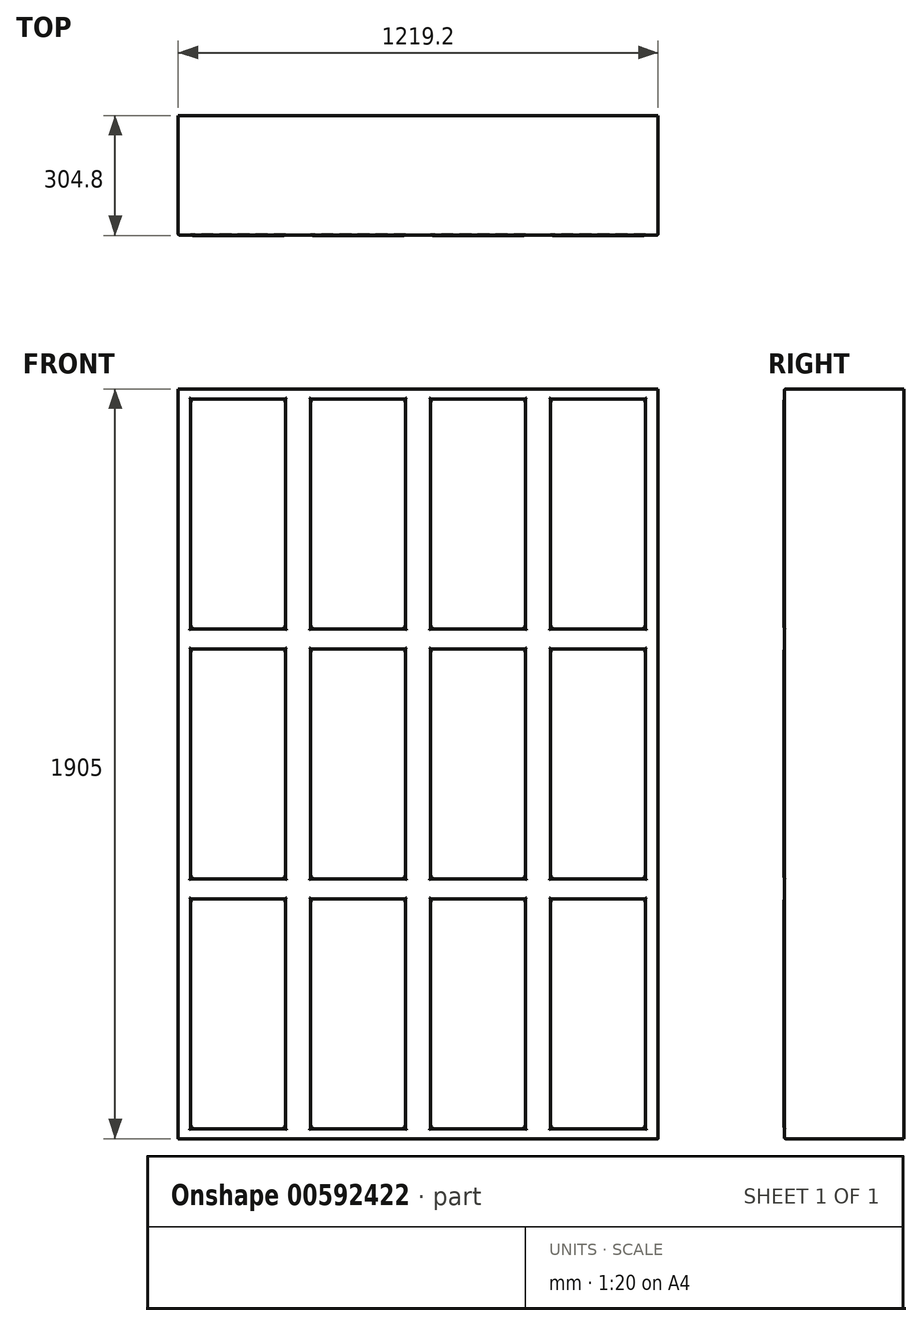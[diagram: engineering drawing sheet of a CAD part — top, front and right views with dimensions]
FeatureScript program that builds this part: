
annotation { "Feature Type Name" : "Feature", "Feature Type Description" : "" }
export const myFeature = defineFeature(function(context is Context, id is Id, definition is map)
    precondition{}
    {
        {
            var Q0;
            Q0=qCreatedBy(makeId("Top.planeOp"),FACE);
            var sketch = newSketch(context, id + "F0", { "sketchPlane" : qUnion([Q0])});
            skLineSegment(sketch, "E0.bottom", {"start": v(609.6, -148.59) * mm, "end": v(-609.6, -148.6) * mm});
            skLineSegment(sketch, "E0.top", {"start": v(609.6, 148.6) * mm, "end": v(-609.6, 148.59) * mm});
            skLineSegment(sketch, "E0.left", {"start": v(609.6, -148.59) * mm, "end": v(609.6, 148.6) * mm});
            skLineSegment(sketch, "E0.right", {"start": v(-609.6, -148.6) * mm, "end": v(-609.6, 148.59) * mm});
            skPoint(sketch, "E0.middle", {"position": v(0, 0) * mm});
            skSolve(sketch);
        }
        {
            var Q0;
            Q0=makeQuery(id+"F0.imprint","IMPRINT",FACE,{"disambiguationData":[TD([[makeQuery(id+"F0.imprint","IMPRINT",EDGE,{"derivedFrom":sQuery(id+"F0.wireOp",EDGE,"E0.bottom")}),-1.0]])]});
            extrude(context, id + "F1", {"entities" : qUnion([Q0]), "depth" : 1905 * mm, "offsetDistance" : 25.4 * mm});
        }
        {
            var Q0;
            Q0=makeQuery(id+"F1.opExtrude","SWEPT_FACE",FACE,{"disambiguationData":[OSD([sQuery(id+"F0.wireOp",EDGE,"E0.bottom")])]});
            var sketch = newSketch(context, id + "F2", { "sketchPlane" : qUnion([Q0])});
            skLineSegment(sketch, "E1.bottom", {"start": v(-609.6, 1905) * mm, "end": v(-304.8, 1905) * mm});
            skLineSegment(sketch, "E1.top", {"start": v(-609.6, 1270) * mm, "end": v(-304.8, 1270) * mm});
            skLineSegment(sketch, "E1.left", {"start": v(-609.6, 1905) * mm, "end": v(-609.6, 1270) * mm});
            skLineSegment(sketch, "E1.right", {"start": v(-304.8, 1905) * mm, "end": v(-304.8, 1270) * mm});
            skLineSegment(sketch, "E2.bottom", {"start": v(-336.55, 1295.4) * mm, "end": v(-577.85, 1295.4) * mm});
            skLineSegment(sketch, "E2.top", {"start": v(-336.55, 1879.6) * mm, "end": v(-577.85, 1879.6) * mm});
            skLineSegment(sketch, "E2.left", {"start": v(-336.55, 1295.4) * mm, "end": v(-336.55, 1879.6) * mm});
            skLineSegment(sketch, "E2.right", {"start": v(-577.85, 1295.4) * mm, "end": v(-577.85, 1879.6) * mm});
            skPoint(sketch, "E2.middle", {"position": v(-457.2, 1587.5) * mm});
            skPoint(sketch, "E2.middle.positionSnap0", {"position": v(-304.8, 1587.5) * mm});
            skPoint(sketch, "E2.middle.positionSnap1", {"position": v(-457.2, 1270) * mm});
            skPoint(sketch, "E2.centerSnap0", {"position": v(-304.8, 1587.5) * mm});
            skPoint(sketch, "E2.centerSnap1", {"position": v(-457.2, 1270) * mm});
            skLineSegment(sketch, "E3.0.1.0", {"start": v(-304.8, 1270) * mm, "end": v(-304.8, 635) * mm});
            skLineSegment(sketch, "E3.0.1.1", {"start": v(-609.6, 635) * mm, "end": v(-304.8, 635) * mm});
            skLineSegment(sketch, "E3.0.1.2", {"start": v(-336.55, 660.4) * mm, "end": v(-336.55, 1244.6) * mm});
            skLineSegment(sketch, "E3.0.1.3", {"start": v(-577.85, 660.4) * mm, "end": v(-577.85, 1244.6) * mm});
            skLineSegment(sketch, "E3.0.1.4", {"start": v(-336.55, 1244.6) * mm, "end": v(-577.85, 1244.6) * mm});
            skLineSegment(sketch, "E3.0.1.5", {"start": v(-336.55, 660.4) * mm, "end": v(-577.85, 660.4) * mm});
            skLineSegment(sketch, "E3.0.1.7", {"start": v(-609.6, 1270) * mm, "end": v(-609.6, 635) * mm});
            skLineSegment(sketch, "E3.0.2.0", {"start": v(-304.8, 635) * mm, "end": v(-304.8, 0) * mm});
            skLineSegment(sketch, "E3.0.2.1", {"start": v(-609.6, 0) * mm, "end": v(-304.8, 0) * mm});
            skLineSegment(sketch, "E3.0.2.2", {"start": v(-336.55, 25.4) * mm, "end": v(-336.55, 609.6) * mm});
            skLineSegment(sketch, "E3.0.2.3", {"start": v(-577.85, 25.4) * mm, "end": v(-577.85, 609.6) * mm});
            skLineSegment(sketch, "E3.0.2.4", {"start": v(-336.55, 609.6) * mm, "end": v(-577.85, 609.6) * mm});
            skLineSegment(sketch, "E3.0.2.5", {"start": v(-336.55, 25.4) * mm, "end": v(-577.85, 25.4) * mm});
            skLineSegment(sketch, "E3.0.2.6", {"start": v(-609.6, 635) * mm, "end": v(-304.8, 635) * mm});
            skLineSegment(sketch, "E3.0.2.7", {"start": v(-609.6, 635) * mm, "end": v(-609.6, 0) * mm});
            skLineSegment(sketch, "E3.1.0.0", {"start": v(0, 1905) * mm, "end": v(0, 1270) * mm});
            skLineSegment(sketch, "E3.1.0.1", {"start": v(-304.8, 1270) * mm, "end": v(0, 1270) * mm});
            skLineSegment(sketch, "E3.1.0.2", {"start": v(-31.75, 1295.4) * mm, "end": v(-31.75, 1879.6) * mm});
            skLineSegment(sketch, "E3.1.0.3", {"start": v(-273.05, 1295.4) * mm, "end": v(-273.05, 1879.6) * mm});
            skLineSegment(sketch, "E3.1.0.4", {"start": v(-31.75, 1879.6) * mm, "end": v(-273.05, 1879.6) * mm});
            skLineSegment(sketch, "E3.1.0.5", {"start": v(-31.75, 1295.4) * mm, "end": v(-273.05, 1295.4) * mm});
            skLineSegment(sketch, "E3.1.0.6", {"start": v(-304.8, 1905) * mm, "end": v(0, 1905) * mm});
            skLineSegment(sketch, "E3.1.1.0", {"start": v(0, 1270) * mm, "end": v(0, 635) * mm});
            skLineSegment(sketch, "E3.1.1.1", {"start": v(-304.8, 635) * mm, "end": v(0, 635) * mm});
            skLineSegment(sketch, "E3.1.1.2", {"start": v(-31.75, 660.4) * mm, "end": v(-31.75, 1244.6) * mm});
            skLineSegment(sketch, "E3.1.1.3", {"start": v(-273.05, 660.4) * mm, "end": v(-273.05, 1244.6) * mm});
            skLineSegment(sketch, "E3.1.1.4", {"start": v(-31.75, 1244.6) * mm, "end": v(-273.05, 1244.6) * mm});
            skLineSegment(sketch, "E3.1.1.5", {"start": v(-31.75, 660.4) * mm, "end": v(-273.05, 660.4) * mm});
            skLineSegment(sketch, "E3.1.1.6", {"start": v(-304.8, 1270) * mm, "end": v(0, 1270) * mm});
            skLineSegment(sketch, "E3.1.1.7", {"start": v(-304.8, 1270) * mm, "end": v(-304.8, 635) * mm});
            skLineSegment(sketch, "E3.1.2.0", {"start": v(0, 635) * mm, "end": v(0, 0) * mm});
            skLineSegment(sketch, "E3.1.2.1", {"start": v(-304.8, 0) * mm, "end": v(0, 0) * mm});
            skLineSegment(sketch, "E3.1.2.2", {"start": v(-31.75, 25.4) * mm, "end": v(-31.75, 609.6) * mm});
            skLineSegment(sketch, "E3.1.2.3", {"start": v(-273.05, 25.4) * mm, "end": v(-273.05, 609.6) * mm});
            skLineSegment(sketch, "E3.1.2.4", {"start": v(-31.75, 609.6) * mm, "end": v(-273.05, 609.6) * mm});
            skLineSegment(sketch, "E3.1.2.5", {"start": v(-31.75, 25.4) * mm, "end": v(-273.05, 25.4) * mm});
            skLineSegment(sketch, "E3.1.2.6", {"start": v(-304.8, 635) * mm, "end": v(0, 635) * mm});
            skLineSegment(sketch, "E3.1.2.7", {"start": v(-304.8, 635) * mm, "end": v(-304.8, 0) * mm});
            skLineSegment(sketch, "E3.2.0.0", {"start": v(304.8, 1905) * mm, "end": v(304.8, 1270) * mm});
            skLineSegment(sketch, "E3.2.0.1", {"start": v(0, 1270) * mm, "end": v(304.8, 1270) * mm});
            skLineSegment(sketch, "E3.2.0.2", {"start": v(273.05, 1295.4) * mm, "end": v(273.05, 1879.6) * mm});
            skLineSegment(sketch, "E3.2.0.3", {"start": v(31.75, 1295.4) * mm, "end": v(31.75, 1879.6) * mm});
            skLineSegment(sketch, "E3.2.0.4", {"start": v(273.05, 1879.6) * mm, "end": v(31.75, 1879.6) * mm});
            skLineSegment(sketch, "E3.2.0.5", {"start": v(273.05, 1295.4) * mm, "end": v(31.75, 1295.4) * mm});
            skLineSegment(sketch, "E3.2.0.6", {"start": v(0, 1905) * mm, "end": v(304.8, 1905) * mm});
            skLineSegment(sketch, "E3.2.0.7", {"start": v(0, 1905) * mm, "end": v(0, 1270) * mm});
            skLineSegment(sketch, "E3.2.1.0", {"start": v(304.8, 1270) * mm, "end": v(304.8, 635) * mm});
            skLineSegment(sketch, "E3.2.1.1", {"start": v(0, 635) * mm, "end": v(304.8, 635) * mm});
            skLineSegment(sketch, "E3.2.1.2", {"start": v(273.05, 660.4) * mm, "end": v(273.05, 1244.6) * mm});
            skLineSegment(sketch, "E3.2.1.3", {"start": v(31.75, 660.4) * mm, "end": v(31.75, 1244.6) * mm});
            skLineSegment(sketch, "E3.2.1.4", {"start": v(273.05, 1244.6) * mm, "end": v(31.75, 1244.6) * mm});
            skLineSegment(sketch, "E3.2.1.5", {"start": v(273.05, 660.4) * mm, "end": v(31.75, 660.4) * mm});
            skLineSegment(sketch, "E3.2.1.6", {"start": v(0, 1270) * mm, "end": v(304.8, 1270) * mm});
            skLineSegment(sketch, "E3.2.1.7", {"start": v(0, 1270) * mm, "end": v(0, 635) * mm});
            skLineSegment(sketch, "E3.2.2.0", {"start": v(304.8, 635) * mm, "end": v(304.8, 0) * mm});
            skLineSegment(sketch, "E3.2.2.1", {"start": v(0, 0) * mm, "end": v(304.8, 0) * mm});
            skLineSegment(sketch, "E3.2.2.2", {"start": v(273.05, 25.4) * mm, "end": v(273.05, 609.6) * mm});
            skLineSegment(sketch, "E3.2.2.3", {"start": v(31.75, 25.4) * mm, "end": v(31.75, 609.6) * mm});
            skLineSegment(sketch, "E3.2.2.4", {"start": v(273.05, 609.6) * mm, "end": v(31.75, 609.6) * mm});
            skLineSegment(sketch, "E3.2.2.5", {"start": v(273.05, 25.4) * mm, "end": v(31.75, 25.4) * mm});
            skLineSegment(sketch, "E3.2.2.6", {"start": v(0, 635) * mm, "end": v(304.8, 635) * mm});
            skLineSegment(sketch, "E3.2.2.7", {"start": v(0, 635) * mm, "end": v(0, 0) * mm});
            skLineSegment(sketch, "E3.3.0.0", {"start": v(609.6, 1905) * mm, "end": v(609.6, 1270) * mm});
            skLineSegment(sketch, "E3.3.0.1", {"start": v(304.8, 1270) * mm, "end": v(609.6, 1270) * mm});
            skLineSegment(sketch, "E3.3.0.2", {"start": v(577.85, 1295.4) * mm, "end": v(577.85, 1879.6) * mm});
            skLineSegment(sketch, "E3.3.0.3", {"start": v(336.55, 1295.4) * mm, "end": v(336.55, 1879.6) * mm});
            skLineSegment(sketch, "E3.3.0.4", {"start": v(577.85, 1879.6) * mm, "end": v(336.55, 1879.6) * mm});
            skLineSegment(sketch, "E3.3.0.5", {"start": v(577.85, 1295.4) * mm, "end": v(336.55, 1295.4) * mm});
            skLineSegment(sketch, "E3.3.0.6", {"start": v(304.8, 1905) * mm, "end": v(609.6, 1905) * mm});
            skLineSegment(sketch, "E3.3.0.7", {"start": v(304.8, 1905) * mm, "end": v(304.8, 1270) * mm});
            skLineSegment(sketch, "E3.3.1.0", {"start": v(609.6, 1270) * mm, "end": v(609.6, 635) * mm});
            skLineSegment(sketch, "E3.3.1.1", {"start": v(304.8, 635) * mm, "end": v(609.6, 635) * mm});
            skLineSegment(sketch, "E3.3.1.2", {"start": v(577.85, 660.4) * mm, "end": v(577.85, 1244.6) * mm});
            skLineSegment(sketch, "E3.3.1.3", {"start": v(336.55, 660.4) * mm, "end": v(336.55, 1244.6) * mm});
            skLineSegment(sketch, "E3.3.1.4", {"start": v(577.85, 1244.6) * mm, "end": v(336.55, 1244.6) * mm});
            skLineSegment(sketch, "E3.3.1.5", {"start": v(577.85, 660.4) * mm, "end": v(336.55, 660.4) * mm});
            skLineSegment(sketch, "E3.3.1.6", {"start": v(304.8, 1270) * mm, "end": v(609.6, 1270) * mm});
            skLineSegment(sketch, "E3.3.1.7", {"start": v(304.8, 1270) * mm, "end": v(304.8, 635) * mm});
            skLineSegment(sketch, "E3.3.2.0", {"start": v(609.6, 635) * mm, "end": v(609.6, 0) * mm});
            skLineSegment(sketch, "E3.3.2.1", {"start": v(304.8, 0) * mm, "end": v(609.6, 0) * mm});
            skLineSegment(sketch, "E3.3.2.2", {"start": v(577.85, 25.4) * mm, "end": v(577.85, 609.6) * mm});
            skLineSegment(sketch, "E3.3.2.3", {"start": v(336.55, 25.4) * mm, "end": v(336.55, 609.6) * mm});
            skLineSegment(sketch, "E3.3.2.4", {"start": v(577.85, 609.6) * mm, "end": v(336.55, 609.6) * mm});
            skLineSegment(sketch, "E3.3.2.5", {"start": v(577.85, 25.4) * mm, "end": v(336.55, 25.4) * mm});
            skLineSegment(sketch, "E3.3.2.6", {"start": v(304.8, 635) * mm, "end": v(609.6, 635) * mm});
            skLineSegment(sketch, "E3.3.2.7", {"start": v(304.8, 635) * mm, "end": v(304.8, 0) * mm});
            skLineSegment(sketch, "E3.direction1", {"start": v(-609.6, 1270) * mm, "end": v(-304.8, 1270) * mm, "construction": true});
            skLineSegment(sketch, "E3.direction2", {"start": v(-609.6, 1270) * mm, "end": v(-609.6, 635) * mm, "construction": true});
            skSolve(sketch);
        }
        {
            var Q0;
            Q0=makeQuery(id+"F2.imprint","IMPRINT",FACE,{"disambiguationData":[TD([[makeQuery(id+"F2.imprint","IMPRINT",EDGE,{"derivedFrom":sQuery(id+"F2.wireOp",EDGE,"E1.bottom")}),1.0]])]});
            var Q1;
            Q1=makeQuery(id+"F2.imprint","IMPRINT",FACE,{"disambiguationData":[TD([[makeQuery(id+"F2.imprint","IMPRINT",EDGE,{"derivedFrom":sQuery(id+"F2.wireOp",EDGE,"E3.1.0.2")}),-1.0]])]});
            var Q2;
            Q2=makeQuery(id+"F2.imprint","IMPRINT",FACE,{"disambiguationData":[TD([[makeQuery(id+"F2.imprint","IMPRINT",EDGE,{"derivedFrom":sQuery(id+"F2.wireOp",EDGE,"E3.2.0.2")}),-1.0]])]});
            var Q3;
            Q3=makeQuery(id+"F2.imprint","IMPRINT",FACE,{"disambiguationData":[TD([[makeQuery(id+"F2.imprint","IMPRINT",EDGE,{"derivedFrom":sQuery(id+"F2.wireOp",EDGE,"E3.3.0.0")}),-1.0]])]});
            var Q4;
            Q4=makeQuery(id+"F2.imprint","IMPRINT",FACE,{"disambiguationData":[TD([[makeQuery(id+"F2.imprint","IMPRINT",EDGE,{"derivedFrom":sQuery(id+"F2.wireOp",EDGE,"E3.3.1.0")}),-1.0]])]});
            var Q5;
            Q5=makeQuery(id+"F2.imprint","IMPRINT",FACE,{"disambiguationData":[TD([[makeQuery(id+"F2.imprint","IMPRINT",EDGE,{"derivedFrom":sQuery(id+"F2.wireOp",EDGE,"E3.0.1.2")}),-1.0]])]});
            var Q6;
            Q6=makeQuery(id+"F2.imprint","IMPRINT",FACE,{"disambiguationData":[TD([[makeQuery(id+"F2.imprint","IMPRINT",EDGE,{"derivedFrom":sQuery(id+"F2.wireOp",EDGE,"E3.1.1.2")}),-1.0]])]});
            var Q7;
            Q7=makeQuery(id+"F2.imprint","IMPRINT",FACE,{"disambiguationData":[TD([[makeQuery(id+"F2.imprint","IMPRINT",EDGE,{"derivedFrom":sQuery(id+"F2.wireOp",EDGE,"E3.2.1.2")}),-1.0]])]});
            var Q8;
            Q8=makeQuery(id+"F2.imprint","IMPRINT",FACE,{"disambiguationData":[TD([[makeQuery(id+"F2.imprint","IMPRINT",EDGE,{"derivedFrom":sQuery(id+"F2.wireOp",EDGE,"E3.3.2.0")}),-1.0]])]});
            var Q9;
            Q9=makeQuery(id+"F2.imprint","IMPRINT",FACE,{"disambiguationData":[TD([[makeQuery(id+"F2.imprint","IMPRINT",EDGE,{"derivedFrom":sQuery(id+"F2.wireOp",EDGE,"E3.2.2.1")}),-1.0]])]});
            var Q10;
            Q10=makeQuery(id+"F2.imprint","IMPRINT",FACE,{"disambiguationData":[TD([[makeQuery(id+"F2.imprint","IMPRINT",EDGE,{"derivedFrom":sQuery(id+"F2.wireOp",EDGE,"E3.1.2.1")}),-1.0]])]});
            var Q11;
            Q11=makeQuery(id+"F2.imprint","IMPRINT",FACE,{"disambiguationData":[TD([[makeQuery(id+"F2.imprint","IMPRINT",EDGE,{"derivedFrom":sQuery(id+"F2.wireOp",EDGE,"E3.0.2.1")}),-1.0]])]});
            extrude(context, id + "F3", {"entities" : qUnion([Q0, Q1, Q2, Q3, Q4, Q5, Q6, Q7, Q8, Q9, Q10, Q11]), "operationType" : NewBodyOperationType.ADD, "depth" : 6.35 * mm, "offsetDistance" : 25.4 * mm});
        }
        {
            var Q0;
            Q0=makeQuery(id+"F3.opExtrude","CAP_FACE",FACE,{"disambiguationData":[OSD([sQuery(id+"F2.wireOp",EDGE,"E1.bottom"),sQuery(id+"F2.wireOp",EDGE,"E1.left"),sQuery(id+"F2.wireOp",EDGE,"E2.bottom"),sQuery(id+"F2.wireOp",EDGE,"E2.top"),sQuery(id+"F2.wireOp",EDGE,"E2.left"),sQuery(id+"F2.wireOp",EDGE,"E2.right"),sQuery(id+"F2.wireOp",EDGE,"E3.0.1.2"),sQuery(id+"F2.wireOp",EDGE,"E3.0.1.3"),sQuery(id+"F2.wireOp",EDGE,"E3.0.1.4"),sQuery(id+"F2.wireOp",EDGE,"E3.0.1.5"),sQuery(id+"F2.wireOp",EDGE,"E3.0.1.7"),sQuery(id+"F2.wireOp",EDGE,"E3.0.2.1"),sQuery(id+"F2.wireOp",EDGE,"E3.0.2.2"),sQuery(id+"F2.wireOp",EDGE,"E3.0.2.3"),sQuery(id+"F2.wireOp",EDGE,"E3.0.2.4"),sQuery(id+"F2.wireOp",EDGE,"E3.0.2.5"),sQuery(id+"F2.wireOp",EDGE,"E3.0.2.7"),sQuery(id+"F2.wireOp",EDGE,"E3.1.0.2"),sQuery(id+"F2.wireOp",EDGE,"E3.1.0.3"),sQuery(id+"F2.wireOp",EDGE,"E3.1.0.4"),sQuery(id+"F2.wireOp",EDGE,"E3.1.0.5"),sQuery(id+"F2.wireOp",EDGE,"E3.1.0.6"),sQuery(id+"F2.wireOp",EDGE,"E3.1.1.2"),sQuery(id+"F2.wireOp",EDGE,"E3.1.1.3"),sQuery(id+"F2.wireOp",EDGE,"E3.1.1.4"),sQuery(id+"F2.wireOp",EDGE,"E3.1.1.5"),sQuery(id+"F2.wireOp",EDGE,"E3.1.2.1"),sQuery(id+"F2.wireOp",EDGE,"E3.1.2.2"),sQuery(id+"F2.wireOp",EDGE,"E3.1.2.3"),sQuery(id+"F2.wireOp",EDGE,"E3.1.2.4"),sQuery(id+"F2.wireOp",EDGE,"E3.1.2.5"),sQuery(id+"F2.wireOp",EDGE,"E3.2.0.2"),sQuery(id+"F2.wireOp",EDGE,"E3.2.0.3"),sQuery(id+"F2.wireOp",EDGE,"E3.2.0.4"),sQuery(id+"F2.wireOp",EDGE,"E3.2.0.5"),sQuery(id+"F2.wireOp",EDGE,"E3.2.0.6"),sQuery(id+"F2.wireOp",EDGE,"E3.2.1.2"),sQuery(id+"F2.wireOp",EDGE,"E3.2.1.3"),sQuery(id+"F2.wireOp",EDGE,"E3.2.1.4"),sQuery(id+"F2.wireOp",EDGE,"E3.2.1.5"),sQuery(id+"F2.wireOp",EDGE,"E3.2.2.1"),sQuery(id+"F2.wireOp",EDGE,"E3.2.2.2"),sQuery(id+"F2.wireOp",EDGE,"E3.2.2.3"),sQuery(id+"F2.wireOp",EDGE,"E3.2.2.4"),sQuery(id+"F2.wireOp",EDGE,"E3.2.2.5"),sQuery(id+"F2.wireOp",EDGE,"E3.3.0.0"),sQuery(id+"F2.wireOp",EDGE,"E3.3.0.2"),sQuery(id+"F2.wireOp",EDGE,"E3.3.0.3"),sQuery(id+"F2.wireOp",EDGE,"E3.3.0.4"),sQuery(id+"F2.wireOp",EDGE,"E3.3.0.5"),sQuery(id+"F2.wireOp",EDGE,"E3.3.0.6"),sQuery(id+"F2.wireOp",EDGE,"E3.3.1.0"),sQuery(id+"F2.wireOp",EDGE,"E3.3.1.2"),sQuery(id+"F2.wireOp",EDGE,"E3.3.1.3"),sQuery(id+"F2.wireOp",EDGE,"E3.3.1.4"),sQuery(id+"F2.wireOp",EDGE,"E3.3.1.5"),sQuery(id+"F2.wireOp",EDGE,"E3.3.2.0"),sQuery(id+"F2.wireOp",EDGE,"E3.3.2.1"),sQuery(id+"F2.wireOp",EDGE,"E3.3.2.2"),sQuery(id+"F2.wireOp",EDGE,"E3.3.2.3"),sQuery(id+"F2.wireOp",EDGE,"E3.3.2.4"),sQuery(id+"F2.wireOp",EDGE,"E3.3.2.5")])],"isStart":false});
            fillet(context, id + "F4", {"entities" : qUnion([Q0]), "radius" : 2.54 * mm, "tangentPropagation" : true, "allowEdgeOverflow" : false});
        }
        {
            var Q0;
            Q0=makeQuery(id+"F3.boolean.opBoolean","SPLIT",FACE,{"disambiguationData":[TD([makeQuery(id+"F3.opExtrude","SWEPT_FACE",FACE,{"disambiguationData":[OSD([sQuery(id+"F2.wireOp",EDGE,"E2.bottom")])]})])],"derivedFrom":makeQuery(id+"F1.opExtrude","SWEPT_FACE",FACE,{"disambiguationData":[OSD([sQuery(id+"F0.wireOp",EDGE,"E0.bottom")])]})});
            var Q1;
            Q1=makeQuery(id+"F3.boolean.opBoolean","SPLIT",FACE,{"disambiguationData":[TD([makeQuery(id+"F3.opExtrude","SWEPT_FACE",FACE,{"disambiguationData":[OSD([sQuery(id+"F2.wireOp",EDGE,"E3.1.0.2")])]})])],"derivedFrom":makeQuery(id+"F1.opExtrude","SWEPT_FACE",FACE,{"disambiguationData":[OSD([sQuery(id+"F0.wireOp",EDGE,"E0.bottom")])]})});
            var Q2;
            Q2=makeQuery(id+"F3.boolean.opBoolean","SPLIT",FACE,{"disambiguationData":[TD([makeQuery(id+"F3.opExtrude","SWEPT_FACE",FACE,{"disambiguationData":[OSD([sQuery(id+"F2.wireOp",EDGE,"E3.2.0.2")])]})])],"derivedFrom":makeQuery(id+"F1.opExtrude","SWEPT_FACE",FACE,{"disambiguationData":[OSD([sQuery(id+"F0.wireOp",EDGE,"E0.bottom")])]})});
            var Q3;
            Q3=makeQuery(id+"F3.boolean.opBoolean","SPLIT",FACE,{"disambiguationData":[TD([makeQuery(id+"F3.opExtrude","SWEPT_FACE",FACE,{"disambiguationData":[OSD([sQuery(id+"F2.wireOp",EDGE,"E3.3.0.2")])]})])],"derivedFrom":makeQuery(id+"F1.opExtrude","SWEPT_FACE",FACE,{"disambiguationData":[OSD([sQuery(id+"F0.wireOp",EDGE,"E0.bottom")])]})});
            var Q4;
            Q4=makeQuery(id+"F3.boolean.opBoolean","SPLIT",FACE,{"disambiguationData":[TD([makeQuery(id+"F3.opExtrude","SWEPT_FACE",FACE,{"disambiguationData":[OSD([sQuery(id+"F2.wireOp",EDGE,"E3.3.1.2")])]})])],"derivedFrom":makeQuery(id+"F1.opExtrude","SWEPT_FACE",FACE,{"disambiguationData":[OSD([sQuery(id+"F0.wireOp",EDGE,"E0.bottom")])]})});
            var Q5;
            Q5=makeQuery(id+"F3.boolean.opBoolean","SPLIT",FACE,{"disambiguationData":[TD([makeQuery(id+"F3.opExtrude","SWEPT_FACE",FACE,{"disambiguationData":[OSD([sQuery(id+"F2.wireOp",EDGE,"E3.2.1.2")])]})])],"derivedFrom":makeQuery(id+"F1.opExtrude","SWEPT_FACE",FACE,{"disambiguationData":[OSD([sQuery(id+"F0.wireOp",EDGE,"E0.bottom")])]})});
            var Q6;
            Q6=makeQuery(id+"F3.boolean.opBoolean","SPLIT",FACE,{"disambiguationData":[TD([makeQuery(id+"F3.opExtrude","SWEPT_FACE",FACE,{"disambiguationData":[OSD([sQuery(id+"F2.wireOp",EDGE,"E3.1.1.2")])]})])],"derivedFrom":makeQuery(id+"F1.opExtrude","SWEPT_FACE",FACE,{"disambiguationData":[OSD([sQuery(id+"F0.wireOp",EDGE,"E0.bottom")])]})});
            var Q7;
            Q7=makeQuery(id+"F3.boolean.opBoolean","SPLIT",FACE,{"disambiguationData":[TD([makeQuery(id+"F3.opExtrude","SWEPT_FACE",FACE,{"disambiguationData":[OSD([sQuery(id+"F2.wireOp",EDGE,"E3.0.1.2")])]})])],"derivedFrom":makeQuery(id+"F1.opExtrude","SWEPT_FACE",FACE,{"disambiguationData":[OSD([sQuery(id+"F0.wireOp",EDGE,"E0.bottom")])]})});
            var Q8;
            Q8=makeQuery(id+"F3.boolean.opBoolean","SPLIT",FACE,{"disambiguationData":[TD([makeQuery(id+"F3.opExtrude","SWEPT_FACE",FACE,{"disambiguationData":[OSD([sQuery(id+"F2.wireOp",EDGE,"E3.0.2.2")])]})])],"derivedFrom":makeQuery(id+"F1.opExtrude","SWEPT_FACE",FACE,{"disambiguationData":[OSD([sQuery(id+"F0.wireOp",EDGE,"E0.bottom")])]})});
            var Q9;
            Q9=makeQuery(id+"F3.boolean.opBoolean","SPLIT",FACE,{"disambiguationData":[TD([makeQuery(id+"F3.opExtrude","SWEPT_FACE",FACE,{"disambiguationData":[OSD([sQuery(id+"F2.wireOp",EDGE,"E3.1.2.2")])]})])],"derivedFrom":makeQuery(id+"F1.opExtrude","SWEPT_FACE",FACE,{"disambiguationData":[OSD([sQuery(id+"F0.wireOp",EDGE,"E0.bottom")])]})});
            var Q10;
            Q10=makeQuery(id+"F3.boolean.opBoolean","SPLIT",FACE,{"disambiguationData":[TD([makeQuery(id+"F3.opExtrude","SWEPT_FACE",FACE,{"disambiguationData":[OSD([sQuery(id+"F2.wireOp",EDGE,"E3.2.2.2")])]})])],"derivedFrom":makeQuery(id+"F1.opExtrude","SWEPT_FACE",FACE,{"disambiguationData":[OSD([sQuery(id+"F0.wireOp",EDGE,"E0.bottom")])]})});
            var Q11;
            Q11=makeQuery(id+"F3.boolean.opBoolean","SPLIT",FACE,{"disambiguationData":[TD([makeQuery(id+"F3.opExtrude","SWEPT_FACE",FACE,{"disambiguationData":[OSD([sQuery(id+"F2.wireOp",EDGE,"E3.3.2.2")])]})])],"derivedFrom":makeQuery(id+"F1.opExtrude","SWEPT_FACE",FACE,{"disambiguationData":[OSD([sQuery(id+"F0.wireOp",EDGE,"E0.bottom")])]})});
            extrude(context, id + "F5", {"entities" : qUnion([Q0, Q1, Q2, Q3, Q4, Q5, Q6, Q7, Q8, Q9, Q10, Q11]), "operationType" : NewBodyOperationType.ADD, "depth" : 7.62 * mm, "offsetDistance" : 25.4 * mm});
        }
        {
            var Q0;
            {var subQ0=sQuery(id+"F0.wireOp",EDGE,"E0.bottom");Q0=makeQuery(id+"F5.opExtrude","CAP_FACE",FACE,{"disambiguationData":[OSD([subQ0]),TDD([makeQuery(id+"F3.boolean.opBoolean","SPLIT",FACE,{"disambiguationData":[TD([makeQuery(id+"F3.opExtrude","SWEPT_FACE",FACE,{"disambiguationData":[OSD([sQuery(id+"F2.wireOp",EDGE,"E2.bottom")])]})])],"derivedFrom":makeQuery(id+"F1.opExtrude","SWEPT_FACE",FACE,{"disambiguationData":[OSD([subQ0])]})})])],"isStart":false});}
            var Q1;
            {var subQ0=sQuery(id+"F0.wireOp",EDGE,"E0.bottom");Q1=makeQuery(id+"F5.opExtrude","CAP_FACE",FACE,{"disambiguationData":[OSD([subQ0]),TDD([makeQuery(id+"F3.boolean.opBoolean","SPLIT",FACE,{"disambiguationData":[TD([makeQuery(id+"F3.opExtrude","SWEPT_FACE",FACE,{"disambiguationData":[OSD([sQuery(id+"F2.wireOp",EDGE,"E3.1.0.2")])]})])],"derivedFrom":makeQuery(id+"F1.opExtrude","SWEPT_FACE",FACE,{"disambiguationData":[OSD([subQ0])]})})])],"isStart":false});}
            var Q2;
            {var subQ0=sQuery(id+"F0.wireOp",EDGE,"E0.bottom");Q2=makeQuery(id+"F5.opExtrude","CAP_FACE",FACE,{"disambiguationData":[OSD([subQ0]),TDD([makeQuery(id+"F3.boolean.opBoolean","SPLIT",FACE,{"disambiguationData":[TD([makeQuery(id+"F3.opExtrude","SWEPT_FACE",FACE,{"disambiguationData":[OSD([sQuery(id+"F2.wireOp",EDGE,"E3.2.0.2")])]})])],"derivedFrom":makeQuery(id+"F1.opExtrude","SWEPT_FACE",FACE,{"disambiguationData":[OSD([subQ0])]})})])],"isStart":false});}
            var Q3;
            {var subQ0=sQuery(id+"F0.wireOp",EDGE,"E0.bottom");Q3=makeQuery(id+"F5.opExtrude","CAP_FACE",FACE,{"disambiguationData":[OSD([subQ0]),TDD([makeQuery(id+"F3.boolean.opBoolean","SPLIT",FACE,{"disambiguationData":[TD([makeQuery(id+"F3.opExtrude","SWEPT_FACE",FACE,{"disambiguationData":[OSD([sQuery(id+"F2.wireOp",EDGE,"E3.3.0.2")])]})])],"derivedFrom":makeQuery(id+"F1.opExtrude","SWEPT_FACE",FACE,{"disambiguationData":[OSD([subQ0])]})})])],"isStart":false});}
            var Q4;
            {var subQ0=sQuery(id+"F0.wireOp",EDGE,"E0.bottom");Q4=makeQuery(id+"F5.opExtrude","CAP_FACE",FACE,{"disambiguationData":[OSD([subQ0]),TDD([makeQuery(id+"F3.boolean.opBoolean","SPLIT",FACE,{"disambiguationData":[TD([makeQuery(id+"F3.opExtrude","SWEPT_FACE",FACE,{"disambiguationData":[OSD([sQuery(id+"F2.wireOp",EDGE,"E3.3.1.2")])]})])],"derivedFrom":makeQuery(id+"F1.opExtrude","SWEPT_FACE",FACE,{"disambiguationData":[OSD([subQ0])]})})])],"isStart":false});}
            var Q5;
            {var subQ0=sQuery(id+"F0.wireOp",EDGE,"E0.bottom");Q5=makeQuery(id+"F5.opExtrude","CAP_FACE",FACE,{"disambiguationData":[OSD([subQ0]),TDD([makeQuery(id+"F3.boolean.opBoolean","SPLIT",FACE,{"disambiguationData":[TD([makeQuery(id+"F3.opExtrude","SWEPT_FACE",FACE,{"disambiguationData":[OSD([sQuery(id+"F2.wireOp",EDGE,"E3.2.1.2")])]})])],"derivedFrom":makeQuery(id+"F1.opExtrude","SWEPT_FACE",FACE,{"disambiguationData":[OSD([subQ0])]})})])],"isStart":false});}
            var Q6;
            {var subQ0=sQuery(id+"F0.wireOp",EDGE,"E0.bottom");Q6=makeQuery(id+"F5.opExtrude","CAP_FACE",FACE,{"disambiguationData":[OSD([subQ0]),TDD([makeQuery(id+"F3.boolean.opBoolean","SPLIT",FACE,{"disambiguationData":[TD([makeQuery(id+"F3.opExtrude","SWEPT_FACE",FACE,{"disambiguationData":[OSD([sQuery(id+"F2.wireOp",EDGE,"E3.1.1.2")])]})])],"derivedFrom":makeQuery(id+"F1.opExtrude","SWEPT_FACE",FACE,{"disambiguationData":[OSD([subQ0])]})})])],"isStart":false});}
            var Q7;
            {var subQ0=sQuery(id+"F0.wireOp",EDGE,"E0.bottom");Q7=makeQuery(id+"F5.opExtrude","CAP_FACE",FACE,{"disambiguationData":[OSD([subQ0]),TDD([makeQuery(id+"F3.boolean.opBoolean","SPLIT",FACE,{"disambiguationData":[TD([makeQuery(id+"F3.opExtrude","SWEPT_FACE",FACE,{"disambiguationData":[OSD([sQuery(id+"F2.wireOp",EDGE,"E3.0.1.2")])]})])],"derivedFrom":makeQuery(id+"F1.opExtrude","SWEPT_FACE",FACE,{"disambiguationData":[OSD([subQ0])]})})])],"isStart":false});}
            var Q8;
            {var subQ0=sQuery(id+"F0.wireOp",EDGE,"E0.bottom");Q8=makeQuery(id+"F5.opExtrude","CAP_FACE",FACE,{"disambiguationData":[OSD([subQ0]),TDD([makeQuery(id+"F3.boolean.opBoolean","SPLIT",FACE,{"disambiguationData":[TD([makeQuery(id+"F3.opExtrude","SWEPT_FACE",FACE,{"disambiguationData":[OSD([sQuery(id+"F2.wireOp",EDGE,"E3.0.2.2")])]})])],"derivedFrom":makeQuery(id+"F1.opExtrude","SWEPT_FACE",FACE,{"disambiguationData":[OSD([subQ0])]})})])],"isStart":false});}
            var Q9;
            {var subQ0=sQuery(id+"F0.wireOp",EDGE,"E0.bottom");Q9=makeQuery(id+"F5.opExtrude","CAP_FACE",FACE,{"disambiguationData":[OSD([subQ0]),TDD([makeQuery(id+"F3.boolean.opBoolean","SPLIT",FACE,{"disambiguationData":[TD([makeQuery(id+"F3.opExtrude","SWEPT_FACE",FACE,{"disambiguationData":[OSD([sQuery(id+"F2.wireOp",EDGE,"E3.1.2.2")])]})])],"derivedFrom":makeQuery(id+"F1.opExtrude","SWEPT_FACE",FACE,{"disambiguationData":[OSD([subQ0])]})})])],"isStart":false});}
            var Q10;
            {var subQ0=sQuery(id+"F0.wireOp",EDGE,"E0.bottom");Q10=makeQuery(id+"F5.opExtrude","CAP_FACE",FACE,{"disambiguationData":[OSD([subQ0]),TDD([makeQuery(id+"F3.boolean.opBoolean","SPLIT",FACE,{"disambiguationData":[TD([makeQuery(id+"F3.opExtrude","SWEPT_FACE",FACE,{"disambiguationData":[OSD([sQuery(id+"F2.wireOp",EDGE,"E3.2.2.2")])]})])],"derivedFrom":makeQuery(id+"F1.opExtrude","SWEPT_FACE",FACE,{"disambiguationData":[OSD([subQ0])]})})])],"isStart":false});}
            var Q11;
            {var subQ0=sQuery(id+"F0.wireOp",EDGE,"E0.bottom");Q11=makeQuery(id+"F5.opExtrude","CAP_FACE",FACE,{"disambiguationData":[OSD([subQ0]),TDD([makeQuery(id+"F3.boolean.opBoolean","SPLIT",FACE,{"disambiguationData":[TD([makeQuery(id+"F3.opExtrude","SWEPT_FACE",FACE,{"disambiguationData":[OSD([sQuery(id+"F2.wireOp",EDGE,"E3.3.2.2")])]})])],"derivedFrom":makeQuery(id+"F1.opExtrude","SWEPT_FACE",FACE,{"disambiguationData":[OSD([subQ0])]})})])],"isStart":false});}
            fillet(context, id + "F6", {"entities" : qUnion([Q0, Q1, Q2, Q3, Q4, Q5, Q6, Q7, Q8, Q9, Q10, Q11]), "radius" : 5.08 * mm, "tangentPropagation" : true, "allowEdgeOverflow" : false});
        }
    });
